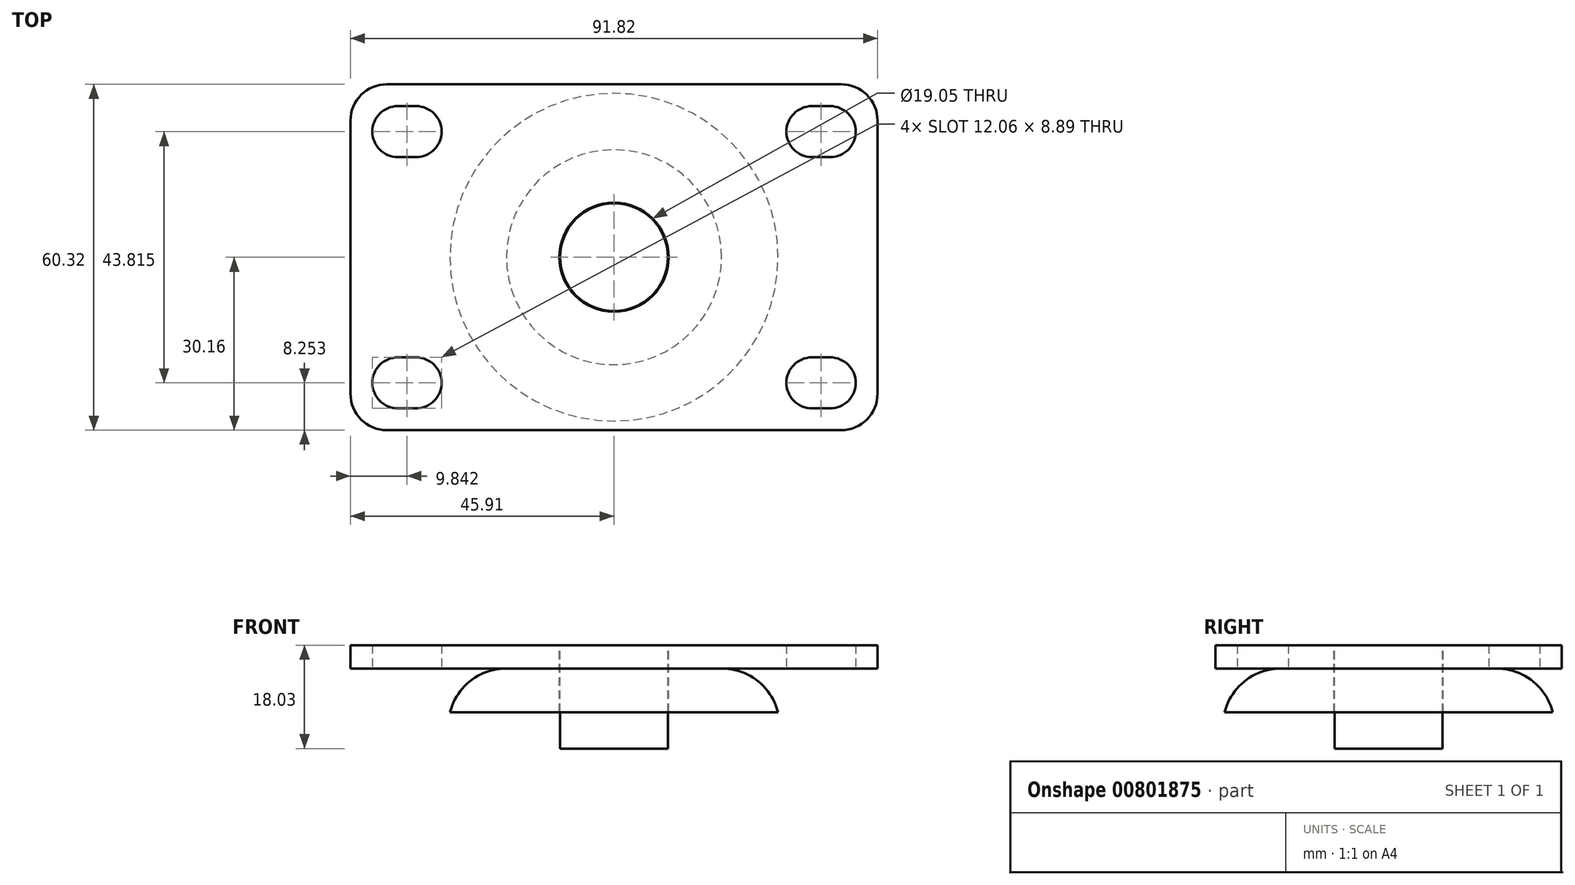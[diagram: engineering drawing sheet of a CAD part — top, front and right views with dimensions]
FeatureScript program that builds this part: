
annotation { "Feature Type Name" : "Feature", "Feature Type Description" : "" }
export const myFeature = defineFeature(function(context is Context, id is Id, definition is map)
    precondition{}
    {
        {
            var Q0;
            Q0=qCreatedBy(makeId("Top.planeOp"),FACE);
            var sketch = newSketch(context, id + "F0", { "sketchPlane" : qUnion([Q0])});
            skLineSegment(sketch, "E0.bottom", {"start": v(-39.56, 30.16) * mm, "end": v(39.56, 30.16) * mm});
            skLineSegment(sketch, "E0.top", {"start": v(-39.56, -30.16) * mm, "end": v(39.56, -30.16) * mm});
            skLineSegment(sketch, "E0.left", {"start": v(-45.91, 23.81) * mm, "end": v(-45.91, -23.81) * mm});
            skLineSegment(sketch, "E0.right", {"start": v(45.91, 23.81) * mm, "end": v(45.91, -23.81) * mm});
            skPoint(sketch, "E0.middle", {"position": v(0, 0) * mm});
            skPoint(sketch, "E1.visualSharp", {"position": v(-45.91, -30.16) * mm});
            skArc(sketch, "E1.filletArc", {"start": v(-45.91, -23.81) * mm, "mid": v(-44.05, -28.3) * mm, "end": v(-39.56, -30.16) * mm});
            skPoint(sketch, "E2.visualSharp", {"position": v(-45.91, 30.16) * mm});
            skArc(sketch, "E2.filletArc", {"start": v(-39.56, 30.16) * mm, "mid": v(-44.05, 28.3) * mm, "end": v(-45.91, 23.81) * mm});
            skPoint(sketch, "E3.visualSharp", {"position": v(45.91, 30.16) * mm});
            skArc(sketch, "E3.filletArc", {"start": v(45.91, 23.81) * mm, "mid": v(44.05, 28.3) * mm, "end": v(39.56, 30.16) * mm});
            skPoint(sketch, "E4.visualSharp", {"position": v(45.91, -30.16) * mm});
            skArc(sketch, "E4.filletArc", {"start": v(39.56, -30.16) * mm, "mid": v(44.05, -28.3) * mm, "end": v(45.91, -23.81) * mm});
            skCircle(sketch, "E5", {"center": v(37.66, 21.9) * mm, "radius": 4.45 * mm});
            skCircle(sketch, "E6", {"center": v(34.48, 21.9) * mm, "radius": 4.45 * mm});
            skLineSegment(sketch, "E7", {"start": v(34.48, 21.9) * mm, "end": v(37.66, 21.9) * mm, "construction": true});
            skLineSegment(sketch, "E8", {"start": v(34.48, 26.35) * mm, "end": v(37.66, 26.35) * mm});
            skLineSegment(sketch, "E9", {"start": v(34.48, 17.46) * mm, "end": v(37.66, 17.46) * mm});
            skCircle(sketch, "E10.MirrorC", {"center": v(-34.48, 21.9) * mm, "radius": 4.45 * mm});
            skCircle(sketch, "E11.MirrorC", {"center": v(-37.66, 21.9) * mm, "radius": 4.45 * mm});
            skLineSegment(sketch, "E12.MirrorCS", {"start": v(-34.48, 17.46) * mm, "end": v(-37.66, 17.46) * mm});
            skLineSegment(sketch, "E13.MirrorCS", {"start": v(-34.48, 26.35) * mm, "end": v(-37.66, 26.35) * mm});
            skCircle(sketch, "E14.MirrorC", {"center": v(-34.48, -21.9) * mm, "radius": 4.45 * mm});
            skLineSegment(sketch, "E15.MirrorCS", {"start": v(-34.48, -17.46) * mm, "end": v(-37.66, -17.46) * mm});
            skCircle(sketch, "E16.MirrorC", {"center": v(-37.66, -21.9) * mm, "radius": 4.45 * mm});
            skLineSegment(sketch, "E17.MirrorCS", {"start": v(-34.48, -26.35) * mm, "end": v(-37.66, -26.35) * mm});
            skLineSegment(sketch, "E18.MirrorCS", {"start": v(34.48, -17.46) * mm, "end": v(37.66, -17.46) * mm});
            skCircle(sketch, "E19.MirrorC", {"center": v(37.66, -21.9) * mm, "radius": 4.45 * mm});
            skCircle(sketch, "E20.MirrorC", {"center": v(34.48, -21.9) * mm, "radius": 4.45 * mm});
            skLineSegment(sketch, "E21.MirrorCS", {"start": v(34.48, -26.35) * mm, "end": v(37.66, -26.35) * mm});
            skSolve(sketch);
        }
        {
            var Q0;
            Q0=makeQuery(id+"F0.imprint","IMPRINT",FACE,{"disambiguationData":[TD([[makeQuery(id+"F0.imprint","IMPRINT",EDGE,{"derivedFrom":sQuery(id+"F0.wireOp",EDGE,"E0.bottom")}),-1.0]])]});
            extrude(context, id + "F1", {"entities" : qUnion([Q0]), "depth" : 4.06 * mm, "offsetDistance" : 25.4 * mm});
        }
        {
            var Q0;
            Q0=qCreatedBy(makeId("Front.planeOp"),FACE);
            var sketch = newSketch(context, id + "F2", { "sketchPlane" : qUnion([Q0])});
            skLineSegment(sketch, "E22", {"start": v(0, 0) * mm, "end": v(0, -7.62) * mm});
            skLineSegment(sketch, "E23", {"start": v(0, -7.62) * mm, "end": v(28.58, -7.62) * mm});
            skLineSegment(sketch, "E24", {"start": v(0, 0) * mm, "end": v(18.74, 0) * mm});
            skArc(sketch, "E25", {"start": v(28.58, -7.62) * mm, "mid": v(24.96, -2.13) * mm, "end": v(18.74, 0) * mm});
            skSolve(sketch);
        }
        {
            var Q0;
            Q0=makeQuery(id+"F2.imprint","IMPRINT",FACE,{"disambiguationData":[TD([[makeQuery(id+"F2.imprint","IMPRINT",EDGE,{"derivedFrom":sQuery(id+"F2.wireOp",EDGE,"E22")}),1.0]])]});
            var Q1;
            Q1=sQuery(id+"F2.wireOp",EDGE,"E22");
            revolve(context, id + "F3", {"operationType" : NewBodyOperationType.ADD, "surfaceOperationType" : NewSurfaceOperationType.NEW, "entities" : qUnion([Q0]), "axis" : qUnion([Q1]), "revolveType" : RevolveType.FULL});
        }
        {
            var Q0;
            Q0=qCreatedBy(makeId("Top.planeOp"),FACE);
            var sketch = newSketch(context, id + "F4", { "sketchPlane" : qUnion([Q0])});
            skCircle(sketch, "E26", {"center": v(0, 0) * mm, "radius": 9.53 * mm});
            skSolve(sketch);
        }
        {
            var Q0;
            Q0=makeQuery(id+"F4.imprint","IMPRINT",FACE,{"disambiguationData":[TD([[makeQuery(id+"F4.imprint","IMPRINT",EDGE,{"derivedFrom":sQuery(id+"F4.wireOp",EDGE,"E26")}),1.0]])]});
            extrude(context, id + "F5", {"entities" : qUnion([Q0]), "operationType" : NewBodyOperationType.REMOVE, "endBound" : BoundingType.THROUGH_ALL, "oppositeDirection" : true, "depth" : 25.4 * mm, "offsetDistance" : 25.4 * mm, "hasSecondDirection" : true, "secondDirectionBound" : SecondDirectionBoundingType.THROUGH_ALL, "secondDirectionOppositeDirection" : false, "secondDirectionDepth" : 25.4 * mm});
        }
        {
            var Q0;
            Q0=makeQuery(id+"F1.opExtrude","CAP_FACE",FACE,{"disambiguationData":[OSD([sQuery(id+"F0.wireOp",EDGE,"E0.bottom"),sQuery(id+"F0.wireOp",EDGE,"E0.top"),sQuery(id+"F0.wireOp",EDGE,"E0.left"),sQuery(id+"F0.wireOp",EDGE,"E0.right"),sQuery(id+"F0.wireOp",EDGE,"E1.filletArc"),sQuery(id+"F0.wireOp",EDGE,"E2.filletArc"),sQuery(id+"F0.wireOp",EDGE,"E3.filletArc"),sQuery(id+"F0.wireOp",EDGE,"E4.filletArc"),sQuery(id+"F0.wireOp",EDGE,"E5"),sQuery(id+"F0.wireOp",EDGE,"E6"),sQuery(id+"F0.wireOp",EDGE,"E8"),sQuery(id+"F0.wireOp",EDGE,"E9"),sQuery(id+"F0.wireOp",EDGE,"E10.MirrorC"),sQuery(id+"F0.wireOp",EDGE,"E11.MirrorC"),sQuery(id+"F0.wireOp",EDGE,"E12.MirrorCS"),sQuery(id+"F0.wireOp",EDGE,"E13.MirrorCS"),sQuery(id+"F0.wireOp",EDGE,"E14.MirrorC"),sQuery(id+"F0.wireOp",EDGE,"E15.MirrorCS"),sQuery(id+"F0.wireOp",EDGE,"E16.MirrorC"),sQuery(id+"F0.wireOp",EDGE,"E17.MirrorCS"),sQuery(id+"F0.wireOp",EDGE,"E18.MirrorCS"),sQuery(id+"F0.wireOp",EDGE,"E19.MirrorC"),sQuery(id+"F0.wireOp",EDGE,"E20.MirrorC"),sQuery(id+"F0.wireOp",EDGE,"E21.MirrorCS")])],"isStart":false});
            var sketch = newSketch(context, id + "F6", { "sketchPlane" : qUnion([Q0])});
            skCircle(sketch, "E27", {"center": v(0, 0) * mm, "radius": 9.4 * mm});
            skSolve(sketch);
        }
        {
            var Q0;
            Q0=makeQuery(id+"F3.opRevolve","SWEPT_FACE",FACE,{"disambiguationData":[OSD([sQuery(id+"F2.wireOp",EDGE,"E23")])]});
            cPlane(context, id + "F7", {"entities" : qUnion([Q0]), "cplaneType" : CPlaneType.OFFSET, "offset" : 6.35 * mm, "width" : 152.4 * mm, "height" : 152.4 * mm});
        }
        {
            var Q0;
            Q0=makeQuery(id+"F6.imprint","IMPRINT",FACE,{"disambiguationData":[TD([[makeQuery(id+"F6.imprint","IMPRINT",EDGE,{"derivedFrom":sQuery(id+"F6.wireOp",EDGE,"E27")}),1.0]])]});
            var Q1;
            Q1=qCreatedBy(id+"F7.planeOp",FACE);
            extrude(context, id + "F8", {"entities" : qUnion([Q0]), "endBound" : BoundingType.UP_TO_SURFACE, "oppositeDirection" : true, "depth" : 25.4 * mm, "endBoundEntityFace" : qUnion([Q1]), "offsetDistance" : 25.4 * mm});
        }
    });
